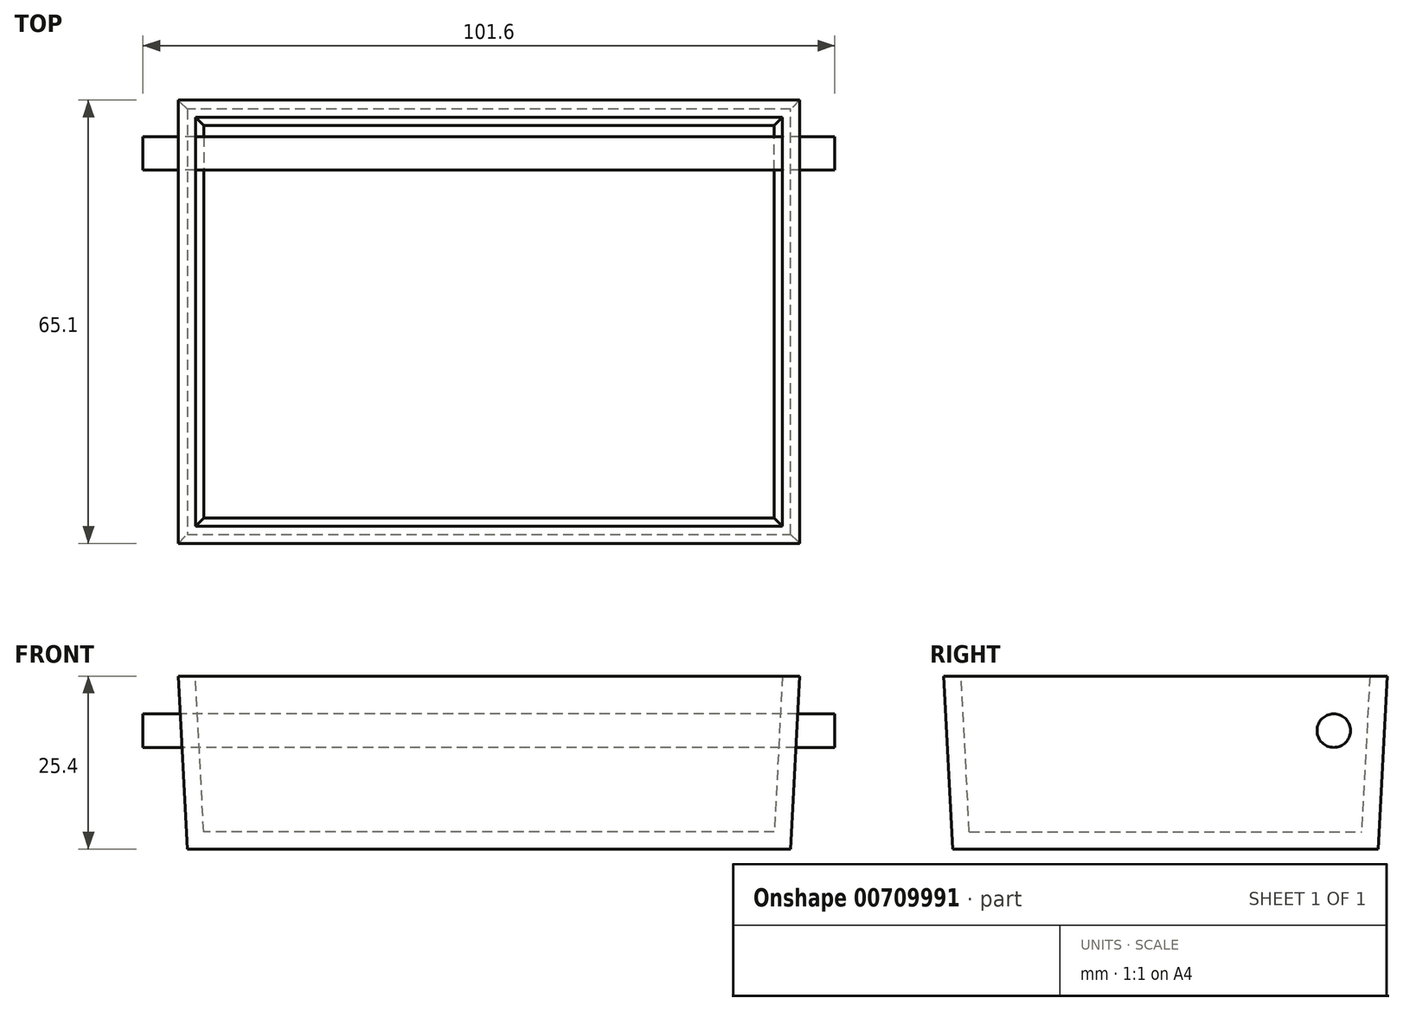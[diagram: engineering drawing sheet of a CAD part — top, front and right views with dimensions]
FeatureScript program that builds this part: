
annotation { "Feature Type Name" : "Feature", "Feature Type Description" : "" }
export const myFeature = defineFeature(function(context is Context, id is Id, definition is map)
    precondition{}
    {
        {
            var Q0;
            Q0=qCreatedBy(makeId("Top.planeOp"),FACE);
            var sketch = newSketch(context, id + "F0", { "sketchPlane" : qUnion([Q0])});
            skLineSegment(sketch, "E0.bottom", {"start": v(45.64, 32.55) * mm, "end": v(-45.64, 32.55) * mm});
            skLineSegment(sketch, "E0.top", {"start": v(45.64, -32.55) * mm, "end": v(-45.64, -32.55) * mm});
            skLineSegment(sketch, "E0.left", {"start": v(45.64, 32.55) * mm, "end": v(45.64, -32.55) * mm});
            skLineSegment(sketch, "E0.right", {"start": v(-45.64, 32.55) * mm, "end": v(-45.64, -32.55) * mm});
            skPoint(sketch, "E0.middle", {"position": v(0, 0) * mm});
            skSolve(sketch);
        }
        {
            var Q0;
            Q0 = qSketchRegion(id + "F0", true);
            extrude(context, id + "F1", {"entities" : qUnion([Q0]), "oppositeDirection" : true, "depth" : 25.4 * mm, "offsetDistance" : 25.4 * mm, "hasDraft" : true, "draftAngle" : 3 * degree, "draftPullDirection" : true});
        }
        {
            var Q0;
            Q0=makeQuery(id+"F1.opExtrude","CAP_FACE",FACE,{"disambiguationData":[OSD([sQuery(id+"F0.wireOp",EDGE,"E0.bottom"),sQuery(id+"F0.wireOp",EDGE,"E0.top"),sQuery(id+"F0.wireOp",EDGE,"E0.left"),sQuery(id+"F0.wireOp",EDGE,"E0.right")])],"isStart":true});
            shell(context, id + "F2", {"entities" : qUnion([Q0]), "thickness" : 2.54 * mm});
        }
        {
            var Q0;
            Q0=qCreatedBy(makeId("Right.planeOp"),FACE);
            var sketch = newSketch(context, id + "F3", { "sketchPlane" : qUnion([Q0])});
            skCircle(sketch, "E1", {"center": v(24.72, -8.01) * mm, "radius": 2.46 * mm});
            skSolve(sketch);
        }
        {
            var Q0;
            Q0 = qSketchRegion(id + "F3", true);
            extrude(context, id + "F4", {"entities" : qUnion([Q0]), "endBound" : BoundingType.SYMMETRIC, "depth" : 101.6 * mm, "offsetDistance" : 25.4 * mm});
        }
    });
